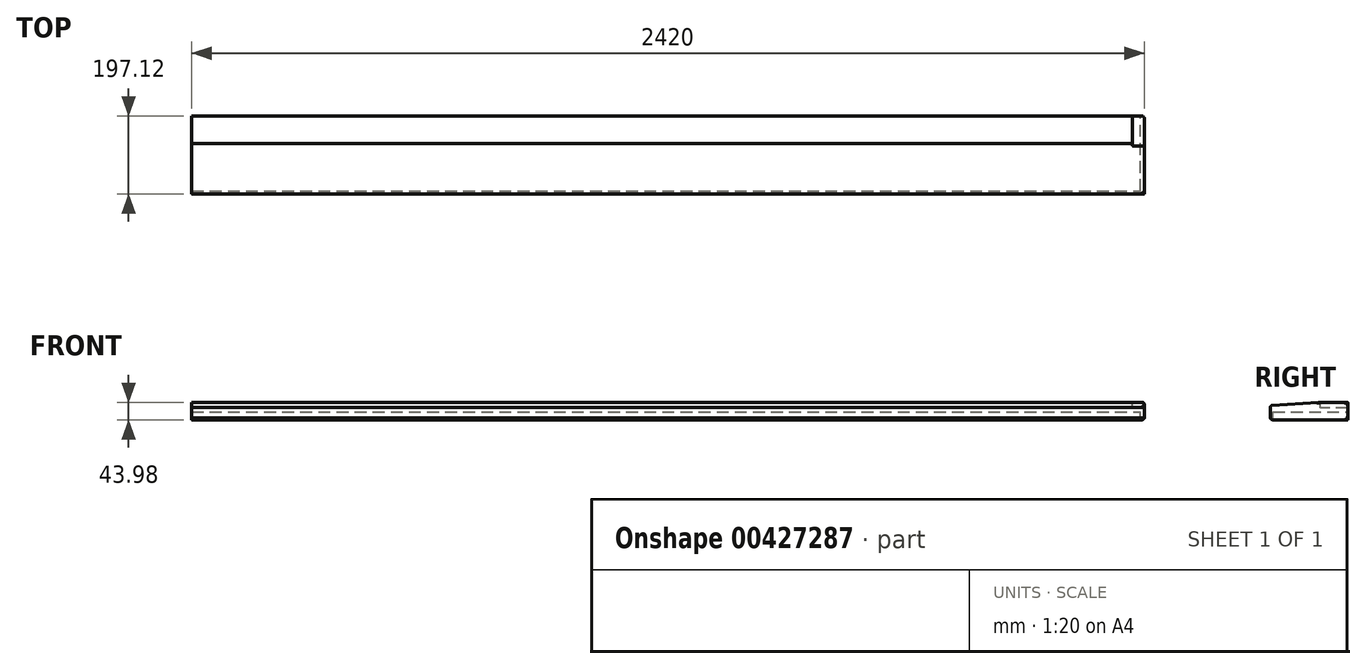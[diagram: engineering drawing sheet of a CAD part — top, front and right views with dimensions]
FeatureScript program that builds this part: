
annotation { "Feature Type Name" : "Feature", "Feature Type Description" : "" }
export const myFeature = defineFeature(function(context is Context, id is Id, definition is map)
    precondition{}
    {
        {
            var Q0;
            Q0=qCreatedBy(makeId("Right.planeOp"),FACE);
            var sketch = newSketch(context, id + "F0", { "sketchPlane" : qUnion([Q0])});
            skLineSegment(sketch, "E0", {"start": v(0, 0) * mm, "end": v(190, 0) * mm});
            skLineSegment(sketch, "E1", {"start": v(-7.12, 10.81) * mm, "end": v(-6.34, -15.77) * mm});
            skLineSegment(sketch, "E2", {"start": v(-1.62, -19.82) * mm, "end": v(0, -19.82) * mm});
            skLineSegment(sketch, "E3", {"start": v(0, -19.82) * mm, "end": v(0, 0) * mm});
            skPoint(sketch, "E4.visualSharp", {"position": v(-8.9, -5.66) * mm});
            skArc(sketch, "E4.filletArc", {"start": v(-6.34, -15.77) * mm, "mid": v(-4.73, -18.67) * mm, "end": v(-1.62, -19.82) * mm});
            skLineSegment(sketch, "E5", {"start": v(114.66, 24.15) * mm, "end": v(-2.47, 16.07) * mm});
            skPoint(sketch, "E6.visualSharp", {"position": v(4.98, 16.59) * mm});
            skArc(sketch, "E6.filletArc", {"start": v(-2.47, 16.07) * mm, "mid": v(-5.87, 14.4) * mm, "end": v(-7.12, 10.81) * mm});
            skLineSegment(sketch, "E7", {"start": v(190, 10) * mm, "end": v(120, 10) * mm});
            skLineSegment(sketch, "E8", {"start": v(190, 0) * mm, "end": v(190, 10) * mm});
            skLineSegment(sketch, "E9", {"start": v(120, 10) * mm, "end": v(120, 19.16) * mm});
            skPoint(sketch, "E10.visualSharp", {"position": v(120, 24.52) * mm});
            skArc(sketch, "E10.filletArc", {"start": v(120, 19.16) * mm, "mid": v(118.41, 22.82) * mm, "end": v(114.66, 24.15) * mm});
            skSolve(sketch);
        }
        {
            var Q0;
            Q0=makeQuery(id+"F0.imprint","IMPRINT",FACE,{"disambiguationData":[TD([[makeQuery(id+"F0.imprint","IMPRINT",EDGE,{"derivedFrom":sQuery(id+"F0.wireOp",EDGE,"E0")}),1.0]])]});
            extrude(context, id + "F1", {"entities" : qUnion([Q0]), "oppositeDirection" : true, "depth" : 2390 * mm});
        }
        {
            var Q0;
            Q0=makeQuery(id+"F1.opExtrude","CAP_FACE",FACE,{"disambiguationData":[OSD([sQuery(id+"F0.wireOp",EDGE,"E0"),sQuery(id+"F0.wireOp",EDGE,"E1"),sQuery(id+"F0.wireOp",EDGE,"E2"),sQuery(id+"F0.wireOp",EDGE,"E3"),sQuery(id+"F0.wireOp",EDGE,"E4.filletArc"),sQuery(id+"F0.wireOp",EDGE,"E5"),sQuery(id+"F0.wireOp",EDGE,"E6.filletArc"),sQuery(id+"F0.wireOp",EDGE,"E7"),sQuery(id+"F0.wireOp",EDGE,"E8"),sQuery(id+"F0.wireOp",EDGE,"E9"),sQuery(id+"F0.wireOp",EDGE,"E10.filletArc")])],"isStart":true});
            var sketch = newSketch(context, id + "F2", { "sketchPlane" : qUnion([Q0])});
            skLineSegment(sketch, "E11.0", {"start": v(-1.62, -19.82) * mm, "end": v(0, -19.82) * mm});
            skArc(sketch, "E11.1", {"start": v(-6.34, -15.77) * mm, "mid": v(-4.73, -18.67) * mm, "end": v(-1.62, -19.82) * mm});
            skLineSegment(sketch, "E11.2", {"start": v(-7.12, 10.81) * mm, "end": v(-6.34, -15.77) * mm});
            skArc(sketch, "E11.3", {"start": v(-2.47, 16.07) * mm, "mid": v(-5.87, 14.4) * mm, "end": v(-7.12, 10.81) * mm});
            skLineSegment(sketch, "E11.4", {"start": v(114.66, 24.15) * mm, "end": v(-2.47, 16.07) * mm});
            skLineSegment(sketch, "E11.5", {"start": v(0, -19.82) * mm, "end": v(0, 0) * mm});
            skLineSegment(sketch, "E11.6", {"start": v(0, 0) * mm, "end": v(190, 0) * mm});
            skLineSegment(sketch, "E11.7", {"start": v(190, 0) * mm, "end": v(190, 10) * mm});
            skLineSegment(sketch, "E12", {"start": v(114.66, 24.15) * mm, "end": v(190, 24.15) * mm});
            skLineSegment(sketch, "E13", {"start": v(190, 24.15) * mm, "end": v(190, 10) * mm});
            skSolve(sketch);
        }
        {
            var Q0;
            Q0=makeQuery(id+"F2.imprint","IMPRINT",FACE,{"disambiguationData":[TD([[makeQuery(id+"F2.imprint","IMPRINT",EDGE,{"derivedFrom":sQuery(id+"F2.wireOp",EDGE,"E11.0")}),1.0]])]});
            var Q1;
            {var subQ1=sQuery(id+"F2.wireOp",EDGE,"E13");Q1=makeQuery(id+"F2.imprint","IMPRINT",FACE,{"disambiguationData":[TD([[makeQuery(id+"F2.imprint","IMPRINT",EDGE,{"derivedFrom":subQ1}),-1.0]])]});}
            extrude(context, id + "F3", {"entities" : qUnion([Q0, Q1]), "operationType" : NewBodyOperationType.ADD, "depth" : 20 * mm});
        }
        {
            var Q0;
            Q0=makeQuery(id+"F3.opExtrude","CAP_FACE",FACE,{"disambiguationData":[OSD([sQuery(id+"F2.wireOp",EDGE,"E11.0"),sQuery(id+"F2.wireOp",EDGE,"E11.1"),sQuery(id+"F2.wireOp",EDGE,"E11.2"),sQuery(id+"F2.wireOp",EDGE,"E11.3"),sQuery(id+"F2.wireOp",EDGE,"E11.4"),sQuery(id+"F2.wireOp",EDGE,"E11.5"),sQuery(id+"F2.wireOp",EDGE,"E11.6"),sQuery(id+"F2.wireOp",EDGE,"E11.7"),sQuery(id+"F2.wireOp",EDGE,"E12"),sQuery(id+"F2.wireOp",EDGE,"E13")])],"isStart":false});
            var sketch = newSketch(context, id + "F4", { "sketchPlane" : qUnion([Q0])});
            skLineSegment(sketch, "E14.0", {"start": v(190, 0) * mm, "end": v(190, 24.15) * mm});
            skLineSegment(sketch, "E14.2", {"start": v(190, 24.15) * mm, "end": v(114.66, 24.15) * mm});
            skLineSegment(sketch, "E14.4", {"start": v(-1.62, -19.82) * mm, "end": v(0, -19.82) * mm});
            skLineSegment(sketch, "E14.5", {"start": v(114.66, 24.15) * mm, "end": v(-2.47, 16.07) * mm});
            skArc(sketch, "E14.6", {"start": v(-2.47, 16.07) * mm, "mid": v(-5.87, 14.4) * mm, "end": v(-7.12, 10.81) * mm});
            skLineSegment(sketch, "E14.7", {"start": v(-7.12, 10.81) * mm, "end": v(-6.34, -15.77) * mm});
            skArc(sketch, "E14.8", {"start": v(-6.34, -15.77) * mm, "mid": v(-4.73, -18.67) * mm, "end": v(-1.62, -19.82) * mm});
            skLineSegment(sketch, "E15", {"start": v(0, -19.82) * mm, "end": v(190, -19.82) * mm});
            skLineSegment(sketch, "E16", {"start": v(190, -19.82) * mm, "end": v(190, 0) * mm});
            skSolve(sketch);
        }
        {
            var Q0;
            Q0=qSketchRegion(id+"F4",true);
            extrude(context, id + "F5", {"entities" : qUnion([Q0]), "operationType" : NewBodyOperationType.ADD, "depth" : 10 * mm});
        }
        {
            var Q0;
            Q0=makeQuery(id+"F5.opExtrude","CAP_EDGE",EDGE,{"disambiguationData":[OSD([sQuery(id+"F4.wireOp",EDGE,"E14.4"),sQuery(id+"F4.wireOp",EDGE,"E15")])],"isStart":false});
            var Q1;
            Q1=makeQuery(id+"F5.opExtrude","CAP_EDGE",EDGE,{"disambiguationData":[OSD([sQuery(id+"F4.wireOp",EDGE,"E14.5")])],"isStart":false});
            var Q2;
            Q2=makeQuery(id+"F5.opExtrude","CAP_EDGE",EDGE,{"disambiguationData":[OSD([sQuery(id+"F4.wireOp",EDGE,"E14.2")])],"isStart":false});
            var Q3;
            Q3=makeQuery(id+"F5.opExtrude","CAP_EDGE",EDGE,{"disambiguationData":[OSD([sQuery(id+"F4.wireOp",EDGE,"E14.0"),sQuery(id+"F4.wireOp",EDGE,"E16")])],"isStart":false});
            fillet(context, id + "F6", {"entities" : qUnion([Q0, Q1, Q2, Q3]), "radius" : 5 * mm, "tangentPropagation" : true, "allowEdgeOverflow" : false});
        }
    });
